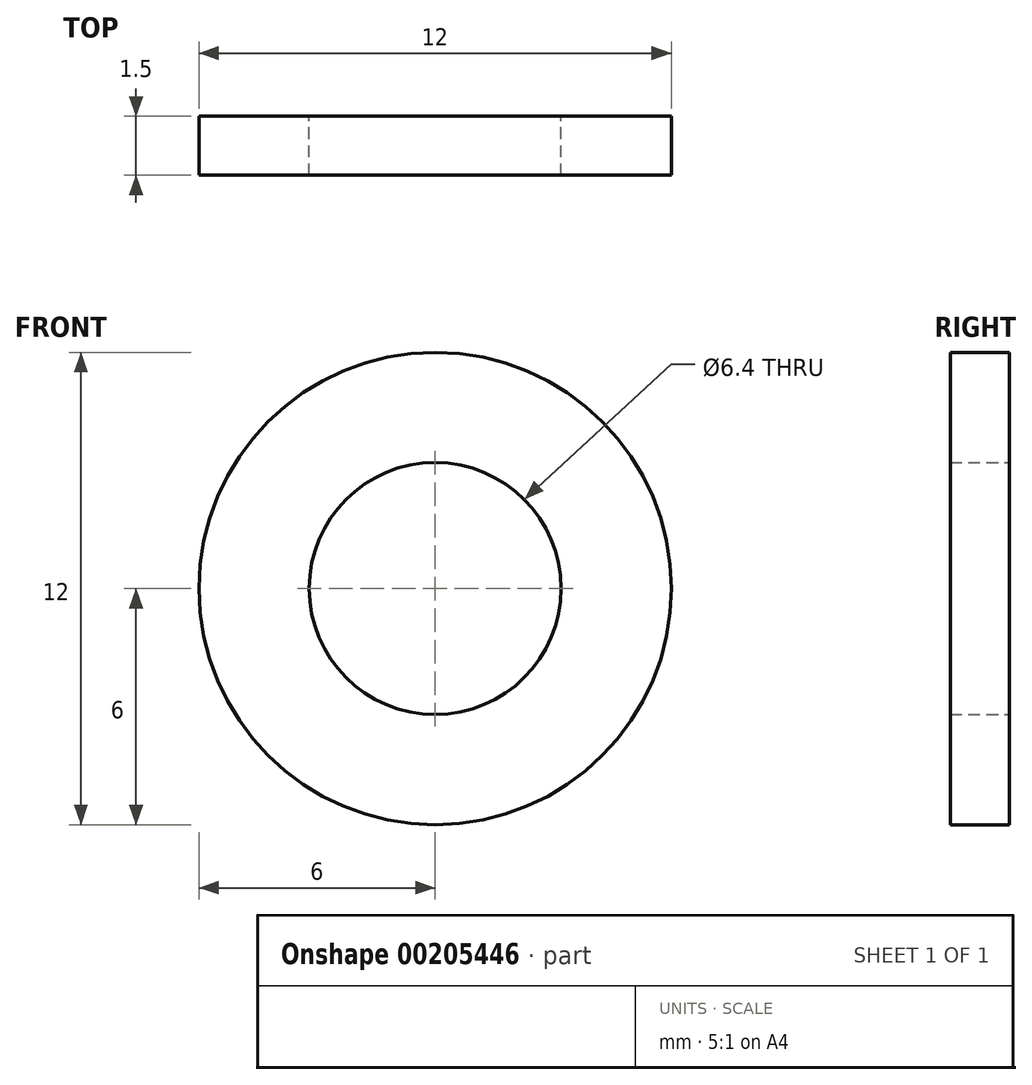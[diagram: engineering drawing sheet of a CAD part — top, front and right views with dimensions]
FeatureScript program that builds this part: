
annotation { "Feature Type Name" : "Feature", "Feature Type Description" : "" }
export const myFeature = defineFeature(function(context is Context, id is Id, definition is map)
    precondition{}
    {
        {
            var Q0;
            Q0=qCreatedBy(makeId("Front.planeOp"),FACE);
            var sketch = newSketch(context, id + "F0", { "sketchPlane" : qUnion([Q0])});
            skCircle(sketch, "E0", {"center": v(0, 0) * mm, "radius": 3.2 * mm});
            skCircle(sketch, "E1", {"center": v(0, 0) * mm, "radius": 6 * mm});
            skSolve(sketch);
        }
        {
            var Q0;
            Q0=makeQuery(id+"F0.imprint","IMPRINT",FACE,{"disambiguationData":[TD([[makeQuery(id+"F0.imprint","IMPRINT",EDGE,{"derivedFrom":sQuery(id+"F0.wireOp",EDGE,"E0")}),-1.0]])]});
            extrude(context, id + "F1", {"entities" : qUnion([Q0]), "depth" : 1.5 * mm});
        }
    });
